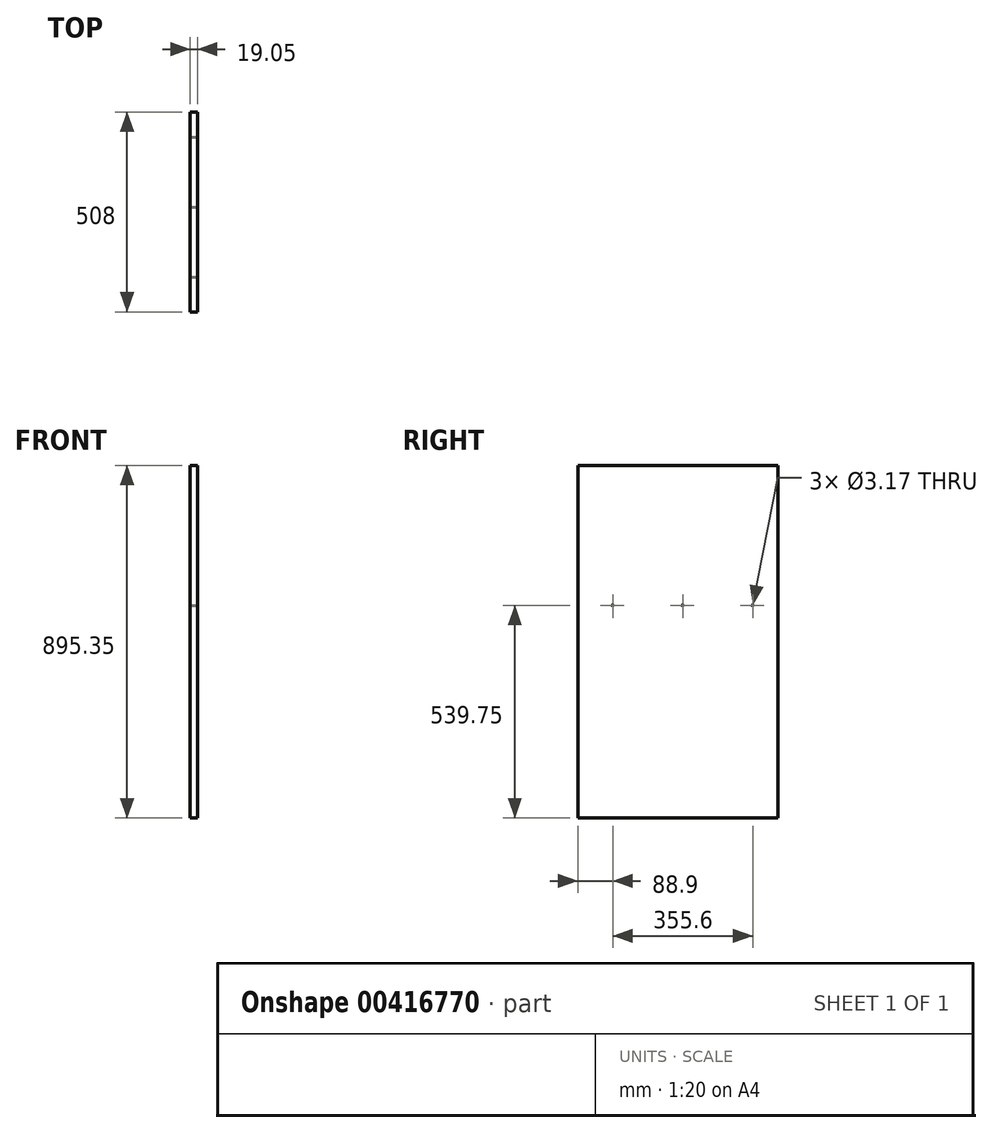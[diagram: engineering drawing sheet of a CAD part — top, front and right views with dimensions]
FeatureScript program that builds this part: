
annotation { "Feature Type Name" : "Feature", "Feature Type Description" : "" }
export const myFeature = defineFeature(function(context is Context, id is Id, definition is map)
    precondition{}
    {
        {
            var Q0;
            Q0=qCreatedBy(makeId("Right.planeOp"),FACE);
            var sketch = newSketch(context, id + "F0", { "sketchPlane" : qUnion([Q0])});
            skLineSegment(sketch, "E0.bottom", {"start": v(0, 0) * mm, "end": v(508, 0) * mm});
            skLineSegment(sketch, "E0.top", {"start": v(0, 895.35) * mm, "end": v(508, 895.35) * mm});
            skLineSegment(sketch, "E0.left", {"start": v(0, 0) * mm, "end": v(0, 895.35) * mm});
            skLineSegment(sketch, "E0.right", {"start": v(508, 0) * mm, "end": v(508, 895.35) * mm});
            skSolve(sketch);
        }
        {
            var Q0;
            Q0 = qSketchRegion(id + "F0", true);
            extrude(context, id + "F1", {"entities" : qUnion([Q0]), "depth" : 19.05 * mm});
        }
        {
            var Q0;
            Q0=makeQuery(id+"F1.opExtrude","CAP_FACE",FACE,{"disambiguationData":[OSD([sQuery(id+"F0.wireOp",EDGE,"E0.bottom"),sQuery(id+"F0.wireOp",EDGE,"E0.top"),sQuery(id+"F0.wireOp",EDGE,"E0.left"),sQuery(id+"F0.wireOp",EDGE,"E0.right")])],"isStart":false});
            var sketch = newSketch(context, id + "F2", { "sketchPlane" : qUnion([Q0])});
            skLineSegment(sketch, "E1", {"start": v(0, 539.75) * mm, "end": v(533.4, 539.75) * mm, "construction": true});
            skCircle(sketch, "E2", {"center": v(88.9, 539.75) * mm, "radius": 1.59 * mm});
            skCircle(sketch, "E3", {"center": v(266.7, 539.75) * mm, "radius": 1.59 * mm});
            skCircle(sketch, "E4", {"center": v(444.5, 539.75) * mm, "radius": 1.59 * mm});
            skSolve(sketch);
        }
        {
            var Q0;
            Q0 = qSketchRegion(id + "F2", true);
            extrude(context, id + "F3", {"entities" : qUnion([Q0]), "operationType" : NewBodyOperationType.REMOVE, "oppositeDirection" : true, "depth" : 25.4 * mm});
        }
    });
